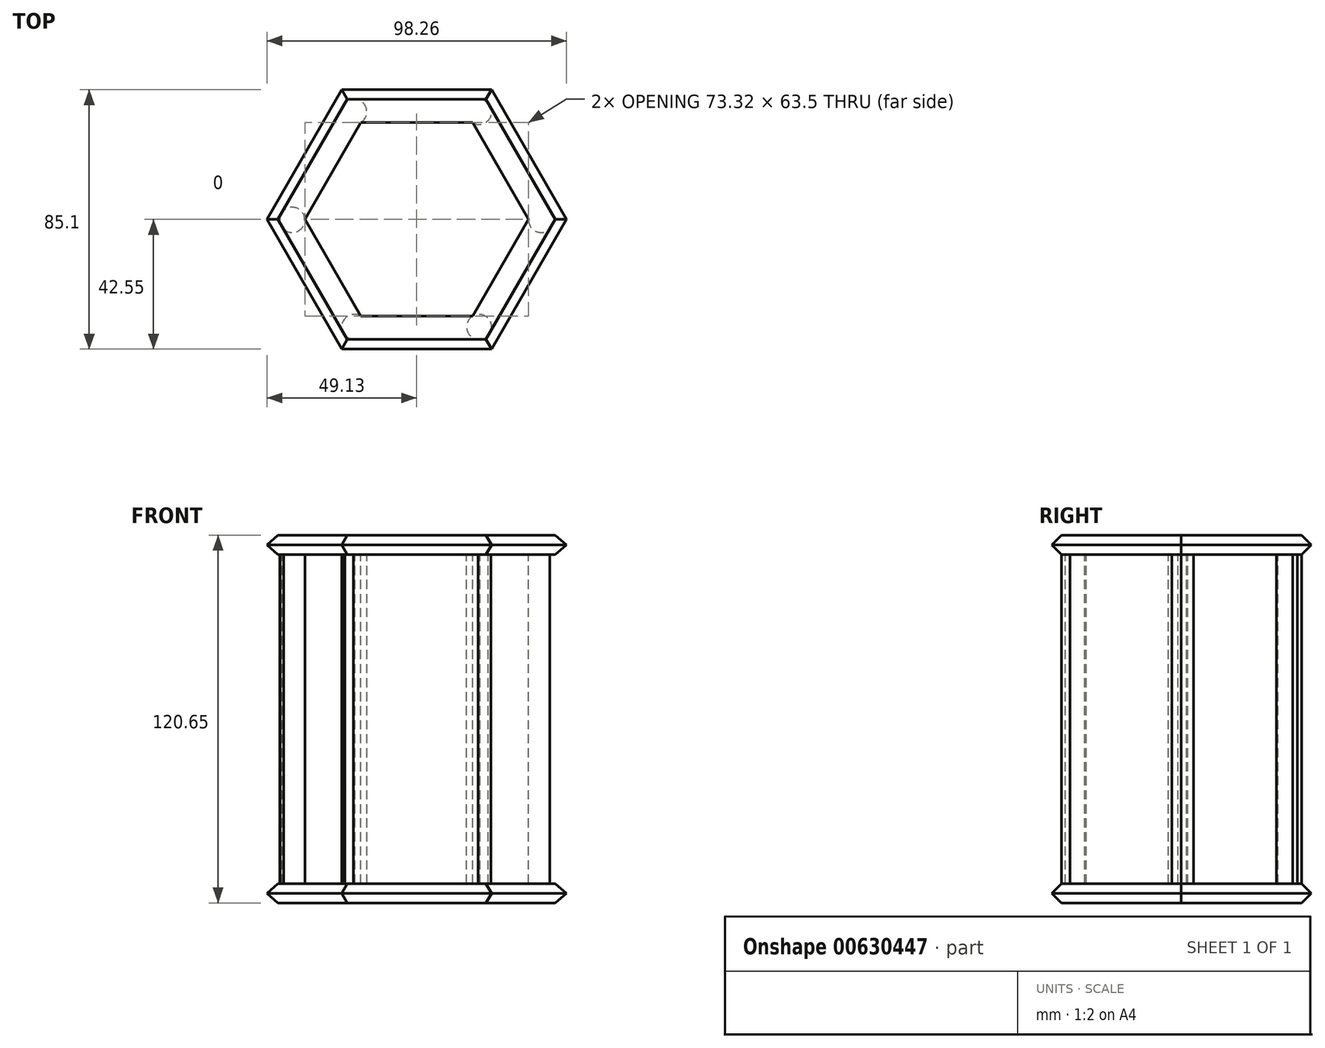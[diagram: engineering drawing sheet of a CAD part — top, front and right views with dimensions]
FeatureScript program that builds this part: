
annotation { "Feature Type Name" : "Feature", "Feature Type Description" : "" }
export const myFeature = defineFeature(function(context is Context, id is Id, definition is map)
    precondition{}
    {
        {
            var Q0;
            Q0=qCreatedBy(makeId("Top.planeOp"),FACE);
            var sketch = newSketch(context, id + "F0", { "sketchPlane" : qUnion([Q0])});
            skCircle(sketch, "E0.cCircle", {"center": v(0, 0) * mm, "radius": 44.45 * mm, "construction": true});
            skLineSegment(sketch, "E0.0", {"start": v(-25.66, 44.45) * mm, "end": v(25.66, 44.45) * mm});
            skLineSegment(sketch, "E0.1", {"start": v(25.66, 44.45) * mm, "end": v(51.33, 0) * mm});
            skLineSegment(sketch, "E0.2", {"start": v(51.33, 0) * mm, "end": v(25.66, -44.45) * mm});
            skLineSegment(sketch, "E0.3", {"start": v(25.66, -44.45) * mm, "end": v(-25.66, -44.45) * mm});
            skLineSegment(sketch, "E0.4", {"start": v(-25.66, -44.45) * mm, "end": v(-51.33, 0) * mm});
            skLineSegment(sketch, "E0.5", {"start": v(-51.33, 0) * mm, "end": v(-25.66, 44.45) * mm});
            skPoint(sketch, "E0.0.midPoint", {"position": v(0, 44.45) * mm});
            skCircle(sketch, "E1.cCircle", {"center": v(0, 0) * mm, "radius": 31.75 * mm, "construction": true});
            skLineSegment(sketch, "E1.0", {"start": v(-18.33, 31.75) * mm, "end": v(18.33, 31.75) * mm});
            skLineSegment(sketch, "E1.1", {"start": v(18.33, 31.75) * mm, "end": v(36.66, 0) * mm});
            skLineSegment(sketch, "E1.2", {"start": v(36.66, 0) * mm, "end": v(18.33, -31.75) * mm});
            skLineSegment(sketch, "E1.3", {"start": v(18.33, -31.75) * mm, "end": v(-18.33, -31.75) * mm});
            skLineSegment(sketch, "E1.4", {"start": v(-18.33, -31.75) * mm, "end": v(-36.66, 0) * mm});
            skLineSegment(sketch, "E1.5", {"start": v(-36.66, 0) * mm, "end": v(-18.33, 31.75) * mm});
            skPoint(sketch, "E1.0.midPoint", {"position": v(0, 31.75) * mm});
            skSolve(sketch);
        }
        {
            var Q0;
            Q0=makeQuery(id+"F0.imprint","IMPRINT",FACE,{"disambiguationData":[TD([[makeQuery(id+"F0.imprint","IMPRINT",EDGE,{"derivedFrom":sQuery(id+"F0.wireOp",EDGE,"E0.0")}),-1.0]])]});
            extrude(context, id + "F1", {"entities" : qUnion([Q0]), "depth" : 6.35 * mm, "offsetDistance" : 25.4 * mm});
        }
        {
            var Q0;
            Q0=makeQuery(id+"F1.opExtrude","CAP_EDGE",EDGE,{"disambiguationData":[OSD([sQuery(id+"F0.wireOp",EDGE,"E0.3")])],"isStart":true});
            var Q1;
            Q1=makeQuery(id+"F1.opExtrude","CAP_EDGE",EDGE,{"disambiguationData":[OSD([sQuery(id+"F0.wireOp",EDGE,"E0.3")])],"isStart":false});
            chamfer(context, id + "F2", {"entities" : qUnion([Q0, Q1]), "width" : 5.08 * mm, "tangentPropagation" : true});
        }
        {
            var Q0;
            Q0=makeQuery(id+"F1.opExtrude","CAP_EDGE",EDGE,{"disambiguationData":[OSD([sQuery(id+"F0.wireOp",EDGE,"E0.2")])],"isStart":true});
            var Q1;
            Q1=makeQuery(id+"F1.opExtrude","CAP_EDGE",EDGE,{"disambiguationData":[OSD([sQuery(id+"F0.wireOp",EDGE,"E0.2")])],"isStart":false});
            chamfer(context, id + "F3", {"entities" : qUnion([Q0, Q1]), "width" : 5.08 * mm, "tangentPropagation" : true});
        }
        {
            var Q0;
            Q0=makeQuery(id+"F1.opExtrude","CAP_EDGE",EDGE,{"disambiguationData":[OSD([sQuery(id+"F0.wireOp",EDGE,"E0.1")])],"isStart":true});
            var Q1;
            Q1=makeQuery(id+"F1.opExtrude","CAP_EDGE",EDGE,{"disambiguationData":[OSD([sQuery(id+"F0.wireOp",EDGE,"E0.1")])],"isStart":false});
            chamfer(context, id + "F4", {"entities" : qUnion([Q0, Q1]), "width" : 5.08 * mm, "tangentPropagation" : true});
        }
        {
            var Q0;
            Q0=makeQuery(id+"F1.opExtrude","CAP_EDGE",EDGE,{"disambiguationData":[OSD([sQuery(id+"F0.wireOp",EDGE,"E0.0")])],"isStart":true});
            var Q1;
            Q1=makeQuery(id+"F1.opExtrude","CAP_EDGE",EDGE,{"disambiguationData":[OSD([sQuery(id+"F0.wireOp",EDGE,"E0.0")])],"isStart":false});
            chamfer(context, id + "F5", {"entities" : qUnion([Q0, Q1]), "width" : 5.08 * mm, "tangentPropagation" : true});
        }
        {
            var Q0;
            Q0=makeQuery(id+"F1.opExtrude","CAP_EDGE",EDGE,{"disambiguationData":[OSD([sQuery(id+"F0.wireOp",EDGE,"E0.5")])],"isStart":true});
            var Q1;
            Q1=makeQuery(id+"F1.opExtrude","CAP_EDGE",EDGE,{"disambiguationData":[OSD([sQuery(id+"F0.wireOp",EDGE,"E0.5")])],"isStart":false});
            chamfer(context, id + "F6", {"entities" : qUnion([Q0, Q1]), "width" : 5.08 * mm, "tangentPropagation" : true});
        }
        {
            var Q0;
            Q0=makeQuery(id+"F1.opExtrude","CAP_EDGE",EDGE,{"disambiguationData":[OSD([sQuery(id+"F0.wireOp",EDGE,"E0.4")])],"isStart":true});
            var Q1;
            Q1=makeQuery(id+"F1.opExtrude","CAP_EDGE",EDGE,{"disambiguationData":[OSD([sQuery(id+"F0.wireOp",EDGE,"E0.4")])],"isStart":false});
            chamfer(context, id + "F7", {"entities" : qUnion([Q0, Q1]), "width" : 5.08 * mm, "tangentPropagation" : true});
        }
        {
            var Q0;
            Q0=makeQuery(id+"F1.opExtrude","CAP_FACE",FACE,{"disambiguationData":[OSD([sQuery(id+"F0.wireOp",EDGE,"E0.0"),sQuery(id+"F0.wireOp",EDGE,"E0.1"),sQuery(id+"F0.wireOp",EDGE,"E0.2"),sQuery(id+"F0.wireOp",EDGE,"E0.3"),sQuery(id+"F0.wireOp",EDGE,"E0.4"),sQuery(id+"F0.wireOp",EDGE,"E0.5"),sQuery(id+"F0.wireOp",EDGE,"E1.0"),sQuery(id+"F0.wireOp",EDGE,"E1.1"),sQuery(id+"F0.wireOp",EDGE,"E1.2"),sQuery(id+"F0.wireOp",EDGE,"E1.3"),sQuery(id+"F0.wireOp",EDGE,"E1.4"),sQuery(id+"F0.wireOp",EDGE,"E1.5")])],"isStart":true});
            var sketch = newSketch(context, id + "F8", { "sketchPlane" : qUnion([Q0])});
            skCircle(sketch, "E2", {"center": v(-40.79, 0.17) * mm, "radius": 4.13 * mm});
            skPoint(sketch, "E2.first.point", {"position": v(-36.66, 0) * mm});
            skPoint(sketch, "E2.second.point", {"position": v(-43.64, 3.16) * mm});
            skPoint(sketch, "E2.third.point", {"position": v(-44.46, -1.74) * mm});
            skCircle(sketch, "E3.MirrorC", {"center": v(40.79, 0.17) * mm, "radius": 4.13 * mm});
            skCircle(sketch, "E4", {"center": v(-20.47, 35.26) * mm, "radius": 4.11 * mm});
            skPoint(sketch, "E4.first.point", {"position": v(-18.33, 31.75) * mm});
            skPoint(sketch, "E4.second.point", {"position": v(-20.2, 39.37) * mm});
            skPoint(sketch, "E4.third.point", {"position": v(-24.4, 36.47) * mm});
            skCircle(sketch, "E5.MirrorC", {"center": v(20.47, 35.26) * mm, "radius": 4.11 * mm});
            skCircle(sketch, "E6.MirrorC", {"center": v(-20.47, -35.26) * mm, "radius": 4.11 * mm});
            skCircle(sketch, "E7.MirrorC", {"center": v(20.47, -35.26) * mm, "radius": 4.11 * mm});
            skSolve(sketch);
        }
        {
            var Q0;
            {var subQ2=sQuery(id+"F0.wireOp",EDGE,"E1.3");var subQ3=makeQuery(id+"F1.opExtrude","CAP_EDGE",EDGE,{"disambiguationData":[OSD([subQ2])],"isStart":true});Q0=makeQuery(id+"F8.imprint","IMPRINT",FACE,{"disambiguationData":[TD([[makeQuery(id+"F8.imprint","IMPRINT",EDGE,{"derivedFrom":subQ3}),-1.0]])]});}
            cPlane(context, id + "F9", {"entities" : qUnion([Q0]), "cplaneType" : CPlaneType.OFFSET, "offset" : 107.95 * mm, "width" : 152.4 * mm, "height" : 152.4 * mm});
        }
        {
            var Q0;
            Q0=qCreatedBy(id+"F9.planeOp",FACE);
            var sketch = newSketch(context, id + "F10", { "sketchPlane" : qUnion([Q0])});
            skCircle(sketch, "E8.cCircle", {"center": v(0, 0) * mm, "radius": 44.45 * mm, "construction": true});
            skLineSegment(sketch, "E8.0", {"start": v(-25.66, 44.45) * mm, "end": v(25.66, 44.45) * mm});
            skLineSegment(sketch, "E8.1", {"start": v(25.66, 44.45) * mm, "end": v(51.33, 0) * mm});
            skLineSegment(sketch, "E8.2", {"start": v(51.33, 0) * mm, "end": v(25.66, -44.45) * mm});
            skLineSegment(sketch, "E8.3", {"start": v(25.66, -44.45) * mm, "end": v(-25.66, -44.45) * mm});
            skLineSegment(sketch, "E8.4", {"start": v(-25.66, -44.45) * mm, "end": v(-51.33, 0) * mm});
            skLineSegment(sketch, "E8.5", {"start": v(-51.33, 0) * mm, "end": v(-25.66, 44.45) * mm});
            skPoint(sketch, "E8.0.midPoint", {"position": v(0, 44.45) * mm});
            skCircle(sketch, "E9.cCircle", {"center": v(0, 0) * mm, "radius": 31.75 * mm, "construction": true});
            skLineSegment(sketch, "E9.0", {"start": v(-18.33, 31.75) * mm, "end": v(18.33, 31.75) * mm});
            skLineSegment(sketch, "E9.1", {"start": v(18.33, 31.75) * mm, "end": v(36.66, 0) * mm});
            skLineSegment(sketch, "E9.2", {"start": v(36.66, 0) * mm, "end": v(18.33, -31.75) * mm});
            skLineSegment(sketch, "E9.3", {"start": v(18.33, -31.75) * mm, "end": v(-18.33, -31.75) * mm});
            skLineSegment(sketch, "E9.4", {"start": v(-18.33, -31.75) * mm, "end": v(-36.66, 0) * mm});
            skLineSegment(sketch, "E9.5", {"start": v(-36.66, 0) * mm, "end": v(-18.33, 31.75) * mm});
            skPoint(sketch, "E9.0.midPoint", {"position": v(0, 31.75) * mm});
            skSolve(sketch);
        }
        {
            var Q0;
            Q0=makeQuery(id+"F10.imprint","IMPRINT",FACE,{"disambiguationData":[TD([[makeQuery(id+"F10.imprint","IMPRINT",EDGE,{"derivedFrom":sQuery(id+"F10.wireOp",EDGE,"E8.0")}),-1.0]])]});
            extrude(context, id + "F11", {"entities" : qUnion([Q0]), "depth" : 6.35 * mm, "offsetDistance" : 25.4 * mm});
        }
        {
            var Q0;
            Q0=makeQuery(id+"F11.opExtrude","CAP_EDGE",EDGE,{"disambiguationData":[OSD([sQuery(id+"F10.wireOp",EDGE,"E8.4")])],"isStart":false});
            var Q1;
            Q1=makeQuery(id+"F11.opExtrude","CAP_EDGE",EDGE,{"disambiguationData":[OSD([sQuery(id+"F10.wireOp",EDGE,"E8.4")])],"isStart":true});
            chamfer(context, id + "F12", {"entities" : qUnion([Q0, Q1]), "width" : 5.08 * mm, "tangentPropagation" : true});
        }
        {
            var Q0;
            Q0=makeQuery(id+"F11.opExtrude","CAP_EDGE",EDGE,{"disambiguationData":[OSD([sQuery(id+"F10.wireOp",EDGE,"E8.5")])],"isStart":false});
            var Q1;
            Q1=makeQuery(id+"F11.opExtrude","CAP_EDGE",EDGE,{"disambiguationData":[OSD([sQuery(id+"F10.wireOp",EDGE,"E8.5")])],"isStart":true});
            chamfer(context, id + "F13", {"entities" : qUnion([Q0, Q1]), "width" : 5.08 * mm, "tangentPropagation" : true});
        }
        {
            var Q0;
            Q0=makeQuery(id+"F11.opExtrude","CAP_EDGE",EDGE,{"disambiguationData":[OSD([sQuery(id+"F10.wireOp",EDGE,"E8.0")])],"isStart":true});
            var Q1;
            Q1=makeQuery(id+"F11.opExtrude","CAP_EDGE",EDGE,{"disambiguationData":[OSD([sQuery(id+"F10.wireOp",EDGE,"E8.0")])],"isStart":false});
            chamfer(context, id + "F14", {"entities" : qUnion([Q0, Q1]), "width" : 5.08 * mm, "tangentPropagation" : true});
        }
        {
            var Q0;
            Q0=makeQuery(id+"F11.opExtrude","CAP_EDGE",EDGE,{"disambiguationData":[OSD([sQuery(id+"F10.wireOp",EDGE,"E8.1")])],"isStart":true});
            var Q1;
            Q1=makeQuery(id+"F11.opExtrude","CAP_EDGE",EDGE,{"disambiguationData":[OSD([sQuery(id+"F10.wireOp",EDGE,"E8.1")])],"isStart":false});
            chamfer(context, id + "F15", {"entities" : qUnion([Q0, Q1]), "width" : 5.08 * mm, "tangentPropagation" : true});
        }
        {
            var Q0;
            Q0=makeQuery(id+"F11.opExtrude","CAP_EDGE",EDGE,{"disambiguationData":[OSD([sQuery(id+"F10.wireOp",EDGE,"E8.2")])],"isStart":true});
            var Q1;
            Q1=makeQuery(id+"F11.opExtrude","CAP_EDGE",EDGE,{"disambiguationData":[OSD([sQuery(id+"F10.wireOp",EDGE,"E8.2")])],"isStart":false});
            chamfer(context, id + "F16", {"entities" : qUnion([Q0, Q1]), "width" : 5.08 * mm, "tangentPropagation" : true});
        }
        {
            var Q0;
            Q0=makeQuery(id+"F11.opExtrude","CAP_EDGE",EDGE,{"disambiguationData":[OSD([sQuery(id+"F10.wireOp",EDGE,"E8.3")])],"isStart":true});
            var Q1;
            Q1=makeQuery(id+"F11.opExtrude","CAP_EDGE",EDGE,{"disambiguationData":[OSD([sQuery(id+"F10.wireOp",EDGE,"E8.3")])],"isStart":false});
            chamfer(context, id + "F17", {"entities" : qUnion([Q0, Q1]), "width" : 5.08 * mm, "tangentPropagation" : true});
        }
        {
            var Q0;
            {var subQ0=sQuery(id+"F8.wireOp",EDGE,"E4");var subQ1=sQuery(id+"F0.wireOp",EDGE,"E1.4");var subQ2=sQuery(id+"F0.wireOp",EDGE,"E1.3");var subQ3=makeQuery(id+"F8.imprint","INTERSECT",VERTEX,{"derivedFrom":[makeQuery(id+"F1.opExtrude","CAP_EDGE",EDGE,{"disambiguationData":[OSD([subQ2])],"isStart":true}),makeQuery(id+"F1.opExtrude","CAP_EDGE",EDGE,{"disambiguationData":[OSD([subQ1])],"isStart":true}),subQ0]});Q0=makeQuery(id+"F8.imprint","IMPRINT",FACE,{"disambiguationData":[TD([[makeQuery(id+"F8.imprint","IMPRINT",EDGE,{"disambiguationData":[TD([[subQ3,1.0]])],"derivedFrom":subQ0}),1.0]])]});}
            var Q1;
            {var subQ0=sQuery(id+"F8.wireOp",EDGE,"E2");var subQ1=sQuery(id+"F0.wireOp",EDGE,"E1.5");var subQ2=sQuery(id+"F0.wireOp",EDGE,"E1.4");var subQ9=makeQuery(id+"F8.imprint","INTERSECT",VERTEX,{"derivedFrom":[makeQuery(id+"F1.opExtrude","CAP_EDGE",EDGE,{"disambiguationData":[OSD([subQ2])],"isStart":true}),makeQuery(id+"F1.opExtrude","CAP_EDGE",EDGE,{"disambiguationData":[OSD([subQ1])],"isStart":true}),subQ0]});Q1=makeQuery(id+"F8.imprint","IMPRINT",FACE,{"disambiguationData":[TD([[makeQuery(id+"F8.imprint","IMPRINT",EDGE,{"disambiguationData":[TD([[subQ9,1.0]])],"derivedFrom":subQ0}),1.0]])]});}
            var Q2;
            {var subQ0=sQuery(id+"F8.wireOp",EDGE,"E5.MirrorC");var subQ1=sQuery(id+"F0.wireOp",EDGE,"E1.3");var subQ2=sQuery(id+"F0.wireOp",EDGE,"E1.2");var subQ9=makeQuery(id+"F8.imprint","INTERSECT",VERTEX,{"derivedFrom":[makeQuery(id+"F1.opExtrude","CAP_EDGE",EDGE,{"disambiguationData":[OSD([subQ2])],"isStart":true}),makeQuery(id+"F1.opExtrude","CAP_EDGE",EDGE,{"disambiguationData":[OSD([subQ1])],"isStart":true}),subQ0]});Q2=makeQuery(id+"F8.imprint","IMPRINT",FACE,{"disambiguationData":[TD([[makeQuery(id+"F8.imprint","IMPRINT",EDGE,{"disambiguationData":[TD([[subQ9,1.0]])],"derivedFrom":subQ0}),-1.0]])]});}
            var Q3;
            {var subQ0=sQuery(id+"F8.wireOp",EDGE,"E3.MirrorC");var subQ1=sQuery(id+"F0.wireOp",EDGE,"E1.2");var subQ2=sQuery(id+"F0.wireOp",EDGE,"E1.1");var subQ9=makeQuery(id+"F8.imprint","INTERSECT",VERTEX,{"derivedFrom":[makeQuery(id+"F1.opExtrude","CAP_EDGE",EDGE,{"disambiguationData":[OSD([subQ2])],"isStart":true}),makeQuery(id+"F1.opExtrude","CAP_EDGE",EDGE,{"disambiguationData":[OSD([subQ1])],"isStart":true}),subQ0]});Q3=makeQuery(id+"F8.imprint","IMPRINT",FACE,{"disambiguationData":[TD([[makeQuery(id+"F8.imprint","IMPRINT",EDGE,{"disambiguationData":[TD([[subQ9,1.0]])],"derivedFrom":subQ0}),-1.0]])]});}
            var Q4;
            {var subQ0=sQuery(id+"F8.wireOp",EDGE,"E7.MirrorC");var subQ1=sQuery(id+"F0.wireOp",EDGE,"E1.1");var subQ2=sQuery(id+"F0.wireOp",EDGE,"E1.0");var subQ9=makeQuery(id+"F8.imprint","INTERSECT",VERTEX,{"derivedFrom":[makeQuery(id+"F1.opExtrude","CAP_EDGE",EDGE,{"disambiguationData":[OSD([subQ2])],"isStart":true}),makeQuery(id+"F1.opExtrude","CAP_EDGE",EDGE,{"disambiguationData":[OSD([subQ1])],"isStart":true}),subQ0]});Q4=makeQuery(id+"F8.imprint","IMPRINT",FACE,{"disambiguationData":[TD([[makeQuery(id+"F8.imprint","IMPRINT",EDGE,{"disambiguationData":[TD([[subQ9,1.0]])],"derivedFrom":subQ0}),1.0]])]});}
            var Q5;
            {var subQ0=sQuery(id+"F8.wireOp",EDGE,"E6.MirrorC");var subQ1=sQuery(id+"F0.wireOp",EDGE,"E1.5");var subQ2=sQuery(id+"F0.wireOp",EDGE,"E1.0");var subQ3=makeQuery(id+"F8.imprint","INTERSECT",VERTEX,{"derivedFrom":[makeQuery(id+"F1.opExtrude","CAP_EDGE",EDGE,{"disambiguationData":[OSD([subQ2])],"isStart":true}),makeQuery(id+"F1.opExtrude","CAP_EDGE",EDGE,{"disambiguationData":[OSD([subQ1])],"isStart":true}),subQ0]});Q5=makeQuery(id+"F8.imprint","IMPRINT",FACE,{"disambiguationData":[TD([[makeQuery(id+"F8.imprint","IMPRINT",EDGE,{"disambiguationData":[TD([[subQ3,1.0]])],"derivedFrom":subQ0}),-1.0]])]});}
            extrude(context, id + "F18", {"entities" : qUnion([Q0, Q1, Q2, Q3, Q4, Q5]), "depth" : 107.95 * mm, "offsetDistance" : 25.4 * mm});
        }
    });
